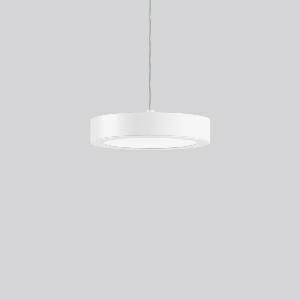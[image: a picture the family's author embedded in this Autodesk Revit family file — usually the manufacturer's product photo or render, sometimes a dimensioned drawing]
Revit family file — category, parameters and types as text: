
# Revit family: toledo_flat_round_p_901686_002_1_76_a86d
name_source: partatom
category: Lighting Fixtures
units: mm (PartAtom-declared; Revit-internal decimal feet)

## family parameters
Cut with Voids When Loaded = No
Host = Face
Light Source = No
Part Type = Normal
Room Calculation Point = No
Round Connector Dimension = Use Diameter
Shared = No

## types (1)
- TOLEDO FLAT round P (1 x LED Modul 840, 2250 lm, 4000)
    Apparent Load = 22 VA
    CIE Flux Codes = 49 80 96 100 100
    Color Rendering = 80
    Color Temperature = 4000
    Default Elevation = 1800 mm
    Description = Series: TOLEDO FLAT
Flat cylindrical pendant luminaire. Cylinder housing sheet steel, powder-coated. Housing: die cast aluminium and sheet steel, powder-coated. Bezel ring: die-cast aluminium, powder-coated. Canopy: sheet steel, powder-coated. Lightguide and diffuser made of non-yellowing plastic (PMMA) opal matt. Suitable for pendant. Transparent suspension cable 2 m, can be shortened. Mounting rings for retrofitting a fabric lampshade available as accessory. 
Colour: white
Diameter: 319 mm
Height: 89 mm
Suspension length: 2000 mm
Lamp: LED
Socket: without socket
Colour temperature: 4000K
Colour rendering index (CRI): 80
System power: 22 W
Rated luminous flux: 2250 lm
Luminous efficiency: 102 lm/W
Control gear: Converter, dimmable, DALI
Protection class: I
Type of protection: IP 20
    Height = 89 mm
    Lamp = 1 x LED Modul 840
    Lamp Light Flux = 2250 lm
    Lamp count = 1
    Length = 319 mm
    Lifetime = 50000 h
    Luminous efficacy = 102 lm/W
    Manufacturer = RZB
    ModVariant = No
    Model = 901686.002.1.76
    Mounting Place = Ceiling
    Mounting Type = Pendant
    Number of Poles = 1
    OnlyDefault = Yes
    Power Factor = 1
    Product Name = TOLEDO FLAT round P
    Product group = Pendant luminaires
    ProductGroupID = 902
    Protection Class = Protection class I
    Protection Degree = IP 20
    RLX_Detail_Level = 1
    RLX_Emergency_Light_Flux = 0 lm
    RLX_Emergency_Type = 0
    RLX_Emergency_Type_DB = No
    RlxData = <blob elided: 71153 chars, md5=0074bc50>
    Socket = socket
    Standby Power = 0 W
    System Light Flux = 2250 lm
    System Power = 22 W
    Type Comments = Product without accessories
    Type Image = 901686.002.jpg
    URL = http://relux.com
    VarID = ---
    Voltage = 230 V
    Voltage Range = 220-240 V
    Weight = 0.00 kg
    Width = 0 mm  [stored 0 ft]

note: [stored X ft] marks values corroborated as IEEE doubles in the binary element streams (Revit-internal decimal feet)

## geometry (parser evidence)
native form markers: Blend x4, Sweep x9
no freeform markers — native parametric forms only
